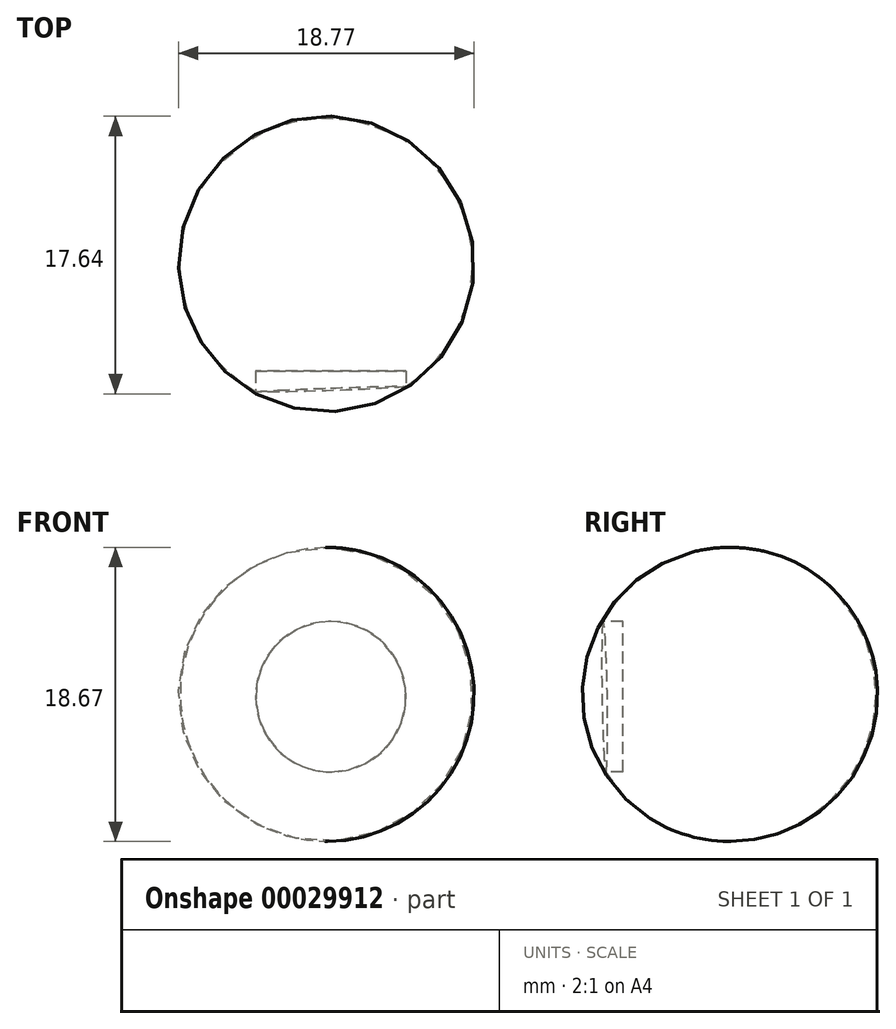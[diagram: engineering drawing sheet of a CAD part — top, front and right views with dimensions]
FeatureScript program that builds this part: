
annotation { "Feature Type Name" : "Feature", "Feature Type Description" : "" }
export const myFeature = defineFeature(function(context is Context, id is Id, definition is map)
    precondition{}
    {
        {
            var Q0;
            Q0=qCreatedBy(makeId("Front.planeOp"),FACE);
            var sketch = newSketch(context, id + "F0", { "sketchPlane" : qUnion([Q0])});
            skLineSegment(sketch, "E0", {"start": v(-43.78, -12.34) * mm, "end": v(-43.78, -31.01) * mm});
            skArc(sketch, "E1", {"start": v(-43.78, -12.34) * mm, "mid": v(-53.07, -21.68) * mm, "end": v(-43.78, -31.01) * mm});
            skSolve(sketch);
        }
        {
            var Q0;
            Q0=makeQuery(id+"F0.imprint","IMPRINT",FACE,{"disambiguationData":[TD([[makeQuery(id+"F0.imprint","IMPRINT",EDGE,{"derivedFrom":sQuery(id+"F0.wireOp",EDGE,"E0")}),-1.0]])]});
            var Q1;
            Q1=sQuery(id+"F0.wireOp",EDGE,"E0");
            revolve(context, id + "F1", {"entities" : qUnion([Q0]), "axis" : qUnion([Q1]), "revolveType" : RevolveType.FULL});
        }
        {
            var Q0;
            Q0=qCreatedBy(makeId("Front.planeOp"),FACE);
            cPlane(context, id + "F2", {"entities" : qUnion([Q0]), "cplaneType" : CPlaneType.OFFSET, "offset" : 9.34 * mm, "width" : 152.4 * mm, "height" : 152.4 * mm});
        }
        {
            var Q0;
            Q0=qCreatedBy(id+"F2.planeOp",FACE);
            var sketch = newSketch(context, id + "F3", { "sketchPlane" : qUnion([Q0])});
            skCircle(sketch, "E2", {"center": v(-43.5, -21.82) * mm, "radius": 4.78 * mm});
            skSolve(sketch);
        }
        {
            var Q0;
            Q0=makeQuery(id+"F3.imprint","IMPRINT",FACE,{"disambiguationData":[TD([[makeQuery(id+"F3.imprint","IMPRINT",EDGE,{"derivedFrom":sQuery(id+"F3.wireOp",EDGE,"E2")}),1.0]])]});
            extrude(context, id + "F4", {"entities" : qUnion([Q0]), "operationType" : NewBodyOperationType.REMOVE, "oppositeDirection" : true, "depth" : 2.54 * mm});
        }
    });
